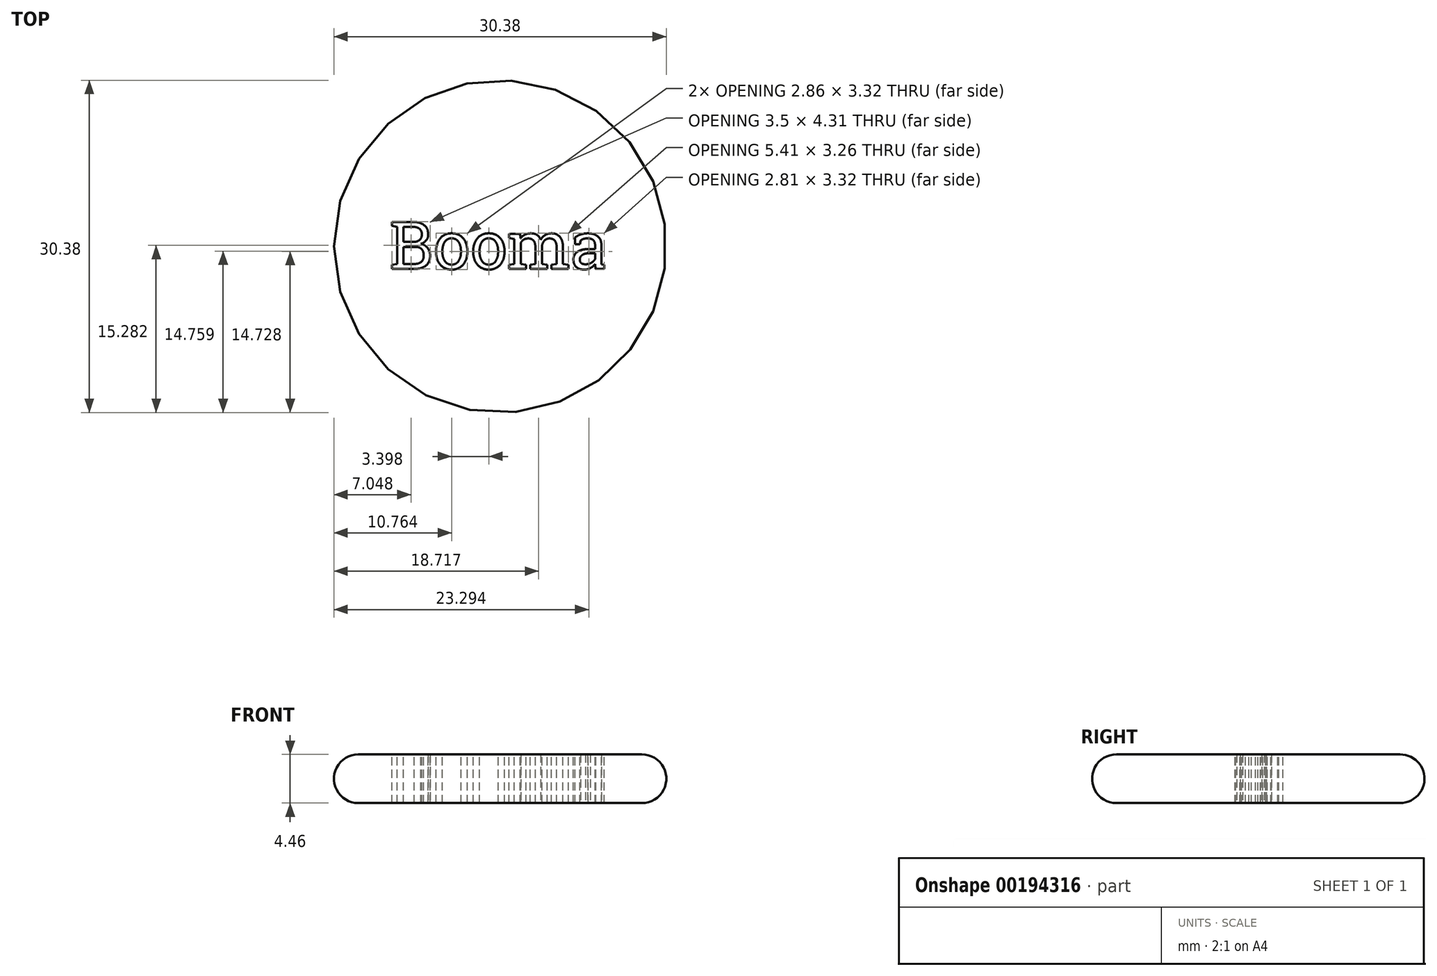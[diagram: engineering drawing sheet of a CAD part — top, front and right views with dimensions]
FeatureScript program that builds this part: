
annotation { "Feature Type Name" : "Feature", "Feature Type Description" : "" }
export const myFeature = defineFeature(function(context is Context, id is Id, definition is map)
    precondition{}
    {
        {
            var Q0;
            Q0=qCreatedBy(makeId("Front.planeOp"),FACE);
            var sketch = newSketch(context, id + "F0", { "sketchPlane" : qUnion([Q0])});
            skLineSegment(sketch, "E0.bottom", {"start": v(0, 0) * mm, "end": v(-12.96, 0) * mm});
            skLineSegment(sketch, "E0.top", {"start": v(0, 4.46) * mm, "end": v(-12.96, 4.46) * mm});
            skLineSegment(sketch, "E0.left", {"start": v(0, 0) * mm, "end": v(0, 4.46) * mm});
            skLineSegment(sketch, "E0.right", {"start": v(-12.96, 0) * mm, "end": v(-12.96, 4.46) * mm});
            skArc(sketch, "E1", {"start": v(-12.96, 4.46) * mm, "mid": v(-15.19, 2.23) * mm, "end": v(-12.96, 0) * mm});
            skSolve(sketch);
        }
        {
            var Q0;
            Q0 = qSketchRegion(id + "F0", true);
            var Q1;
            Q1=sQuery(id+"F0.wireOp",EDGE,"E0.left");
            revolve(context, id + "F1", {"entities" : qUnion([Q0]), "axis" : qUnion([Q1]), "revolveType" : RevolveType.FULL});
        }
        {
            var Q0;
            Q0=qCreatedBy(makeId("Top.planeOp"),FACE);
            cPlane(context, id + "F2", {"entities" : qUnion([Q0]), "cplaneType" : CPlaneType.OFFSET, "offset" : 5 * mm, "width" : 152.4 * mm, "height" : 152.4 * mm});
        }
        {
            var Q0;
            Q0=qCreatedBy(id+"F2.planeOp",FACE);
            var sketch = newSketch(context, id + "F3", { "sketchPlane" : qUnion([Q0])});
            skText(sketch, "E2", { "text": "Booma", "fontName": "RobotoSlab-Regular.ttf"});
            const initialGuessF3  = {"E2": [-0.0101, -0.00206, 1, 0, 0.00436]};
            skSetInitialGuess(sketch, initialGuessF3);
            skSolve(sketch);
        }
        {
            var Q0;
            Q0 = qSketchRegion(id + "F3", true);
            extrude(context, id + "F4", {"entities" : qUnion([Q0]), "operationType" : NewBodyOperationType.REMOVE, "oppositeDirection" : true, "depth" : 25.4 * mm});
        }
    });
